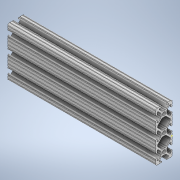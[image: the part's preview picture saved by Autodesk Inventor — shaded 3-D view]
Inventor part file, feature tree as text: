
AUTODESK INVENTOR PART (.ipt)
format: ipt  version: 2020 (Build 240168000, 168)  size: 376,320 bytes
history: native  units: in
note: dims shown in document units (in); Inventor stores cm internally (conversion verified against a paired STEP export)
features: sketch x2, extrude x1
ambient origin geometry x8: Origin, YZ Plane, XZ Plane, XY Plane, X Axis, Y Axis, Z Axis, Center Point
bodies: Solid1 (feature_tree)
feature tree (3):
  extrude  "Extrusion1"  [1 undecoded]
  sketch  "Sketch2"
  sketch  "Sketch1"  dims[d0=9.0in d1=0.0in]
note: 1 required parameter value undecoded (feature->parameter linkage not recoverable at this tier; creation-order binding heuristic only, values carry confidence <= 0.55)
